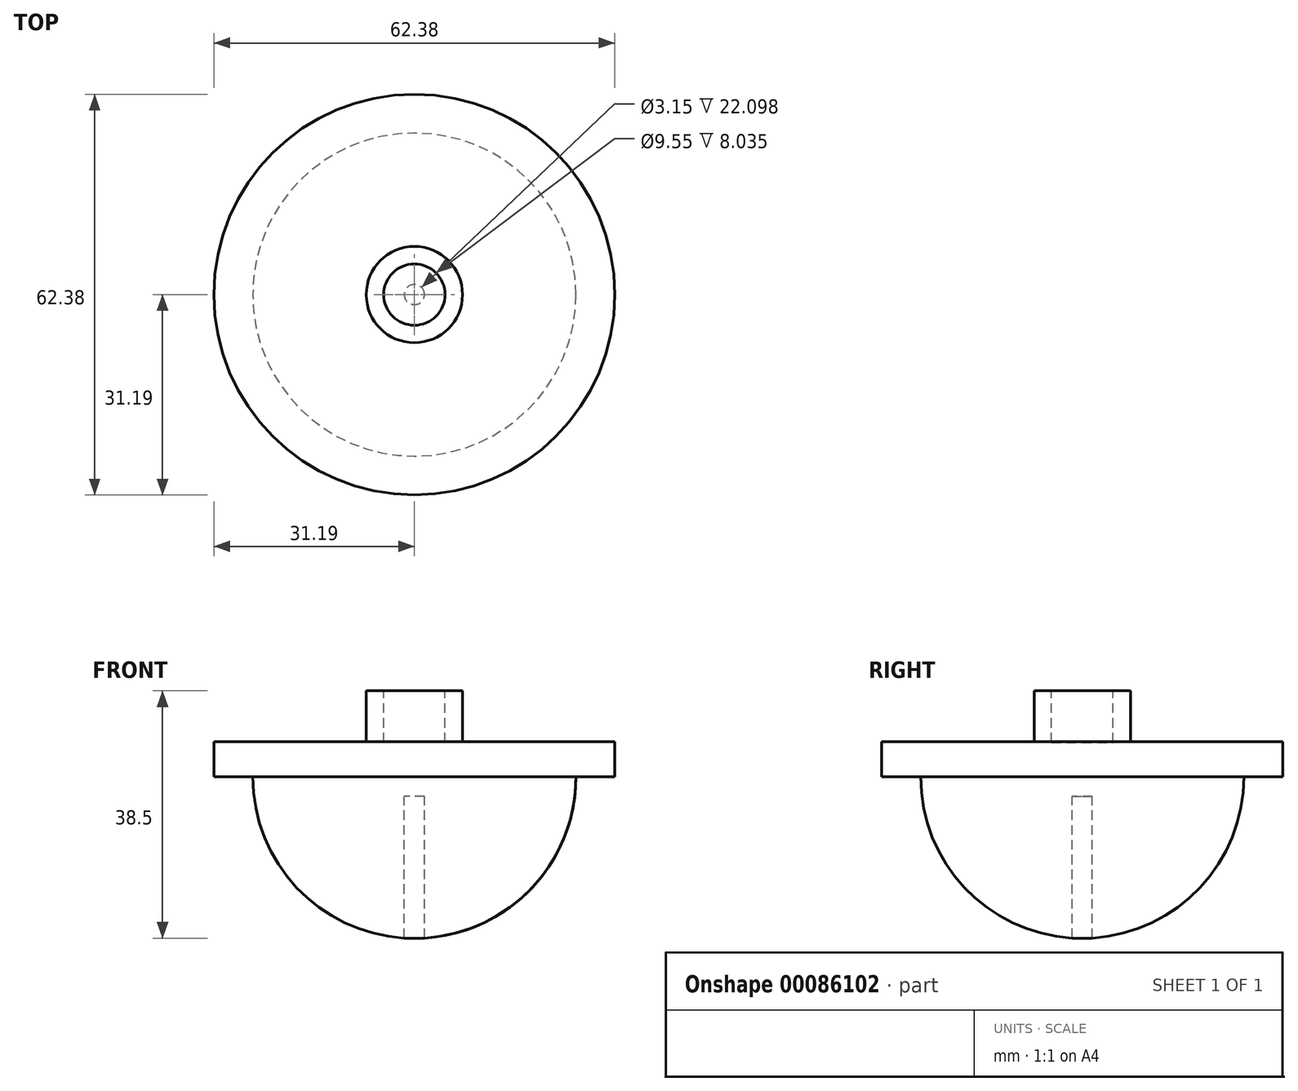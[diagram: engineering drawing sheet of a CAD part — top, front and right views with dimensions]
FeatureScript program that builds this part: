
annotation { "Feature Type Name" : "Feature", "Feature Type Description" : "" }
export const myFeature = defineFeature(function(context is Context, id is Id, definition is map)
    precondition{}
    {
        {
            var Q0;
            Q0=qCreatedBy(makeId("Front.planeOp"),FACE);
            var sketch = newSketch(context, id + "F0", { "sketchPlane" : qUnion([Q0])});
            skPoint(sketch, "E0.center.orphan", {"position": v(0, 27.72) * mm});
            skArc(sketch, "E1", {"start": v(1.57, 2.63) * mm, "mid": v(18.33, 10.5) * mm, "end": v(25.15, 27.72) * mm});
            skPoint(sketch, "E2.orphan", {"position": v(0, 56.8) * mm});
            skPoint(sketch, "E3.end.orphan", {"position": v(0, 42.02) * mm});
            skLineSegment(sketch, "E4", {"start": v(0, 33.1) * mm, "end": v(0, 24.72) * mm});
            skPoint(sketch, "E5.orphan", {"position": v(0, 51.54) * mm});
            skLineSegment(sketch, "E6", {"start": v(1.57, 2.63) * mm, "end": v(1.57, 24.72) * mm});
            skLineSegment(sketch, "E7", {"start": v(1.57, 24.72) * mm, "end": v(0, 24.72) * mm});
            skPoint(sketch, "E8.orphan", {"position": v(37.24, 27.72) * mm});
            skLineSegment(sketch, "E9", {"start": v(25.15, 27.72) * mm, "end": v(31.2, 27.72) * mm});
            skLineSegment(sketch, "E10", {"start": v(0, 33.1) * mm, "end": v(4.78, 33.1) * mm});
            skLineSegment(sketch, "E11", {"start": v(31.2, 27.72) * mm, "end": v(31.2, 33.21) * mm});
            skLineSegment(sketch, "E12", {"start": v(31.2, 33.21) * mm, "end": v(7.5, 33.21) * mm});
            skLineSegment(sketch, "E13", {"start": v(7.5, 33.21) * mm, "end": v(7.5, 41.13) * mm});
            skPoint(sketch, "E14.orphan", {"position": v(0, 38.86) * mm});
            skLineSegment(sketch, "E15", {"start": v(4.78, 33.1) * mm, "end": v(4.78, 41.13) * mm});
            skLineSegment(sketch, "E16", {"start": v(4.78, 41.13) * mm, "end": v(7.5, 41.13) * mm});
            skSolve(sketch);
        }
        {
            var Q0;
            Q0=makeQuery(id+"F0.imprint","IMPRINT",FACE,{"disambiguationData":[TD([[makeQuery(id+"F0.imprint","IMPRINT",EDGE,{"derivedFrom":sQuery(id+"F0.wireOp",EDGE,"E1")}),1.0]])]});
            var Q1;
            Q1=sQuery(id+"F0.wireOp",EDGE,"E4");
            revolve(context, id + "F1", {"entities" : qUnion([Q0]), "axis" : qUnion([Q1]), "revolveType" : RevolveType.FULL});
        }
    });
